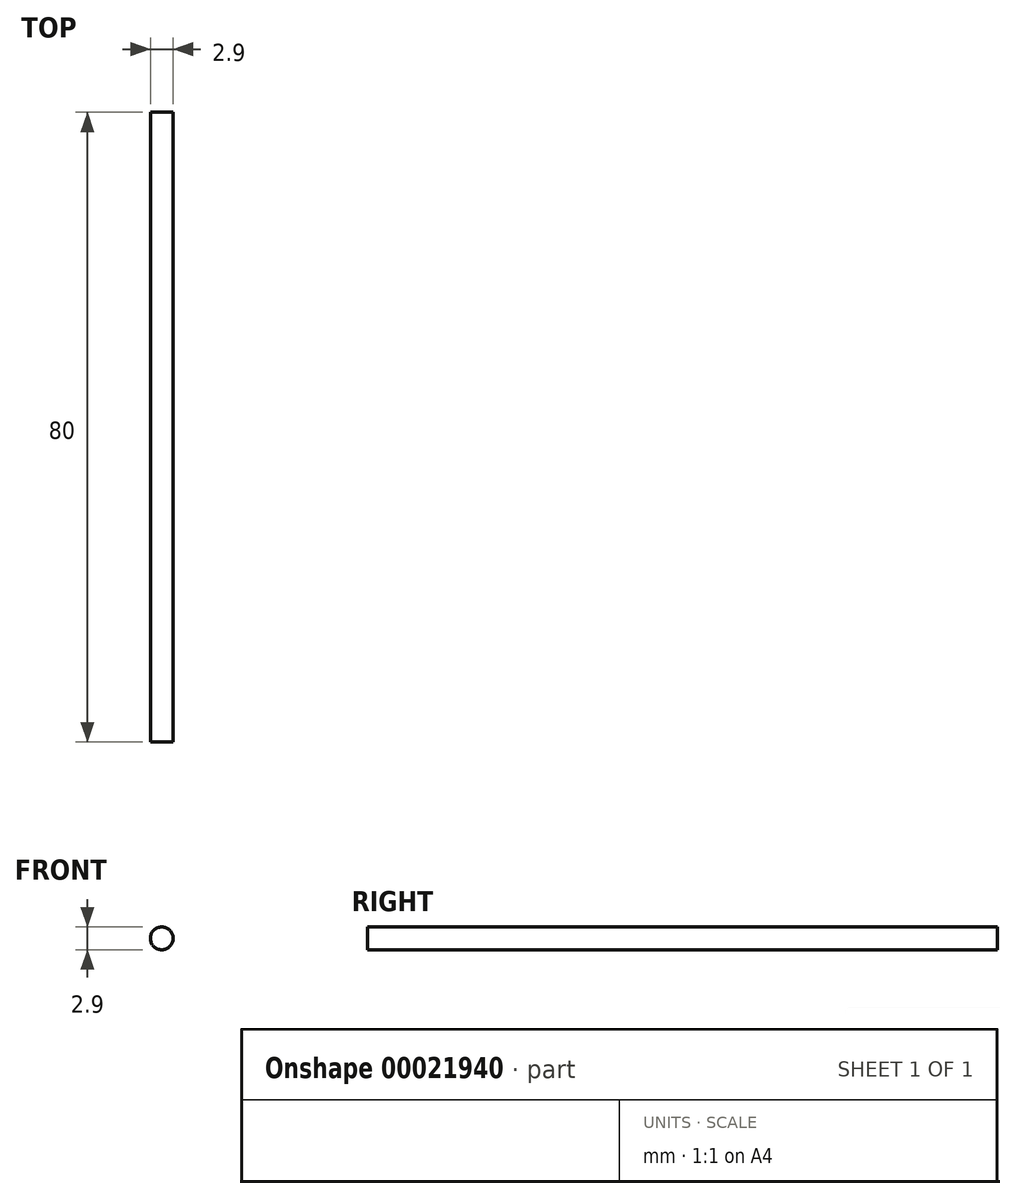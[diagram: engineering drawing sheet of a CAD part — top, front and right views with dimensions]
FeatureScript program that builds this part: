
annotation { "Feature Type Name" : "Feature", "Feature Type Description" : "" }
export const myFeature = defineFeature(function(context is Context, id is Id, definition is map)
    precondition{}
    {
        {
            var Q0;
            Q0=qCreatedBy(makeId("Front.planeOp"),FACE);
            var sketch = newSketch(context, id + "F0", { "sketchPlane" : qUnion([Q0])});
            skCircle(sketch, "E0", {"center": v(0, 0) * mm, "radius": 1.45 * mm});
            skSolve(sketch);
        }
        {
            var Q0;
            Q0=makeQuery(id+"F0.imprint","IMPRINT",FACE,{"disambiguationData":[TD([[makeQuery(id+"F0.imprint","IMPRINT",EDGE,{"derivedFrom":sQuery(id+"F0.wireOp",EDGE,"E0")}),1.0]])]});
            extrude(context, id + "F1", {"entities" : qUnion([Q0]), "depth" : 80 * mm});
        }
    });
